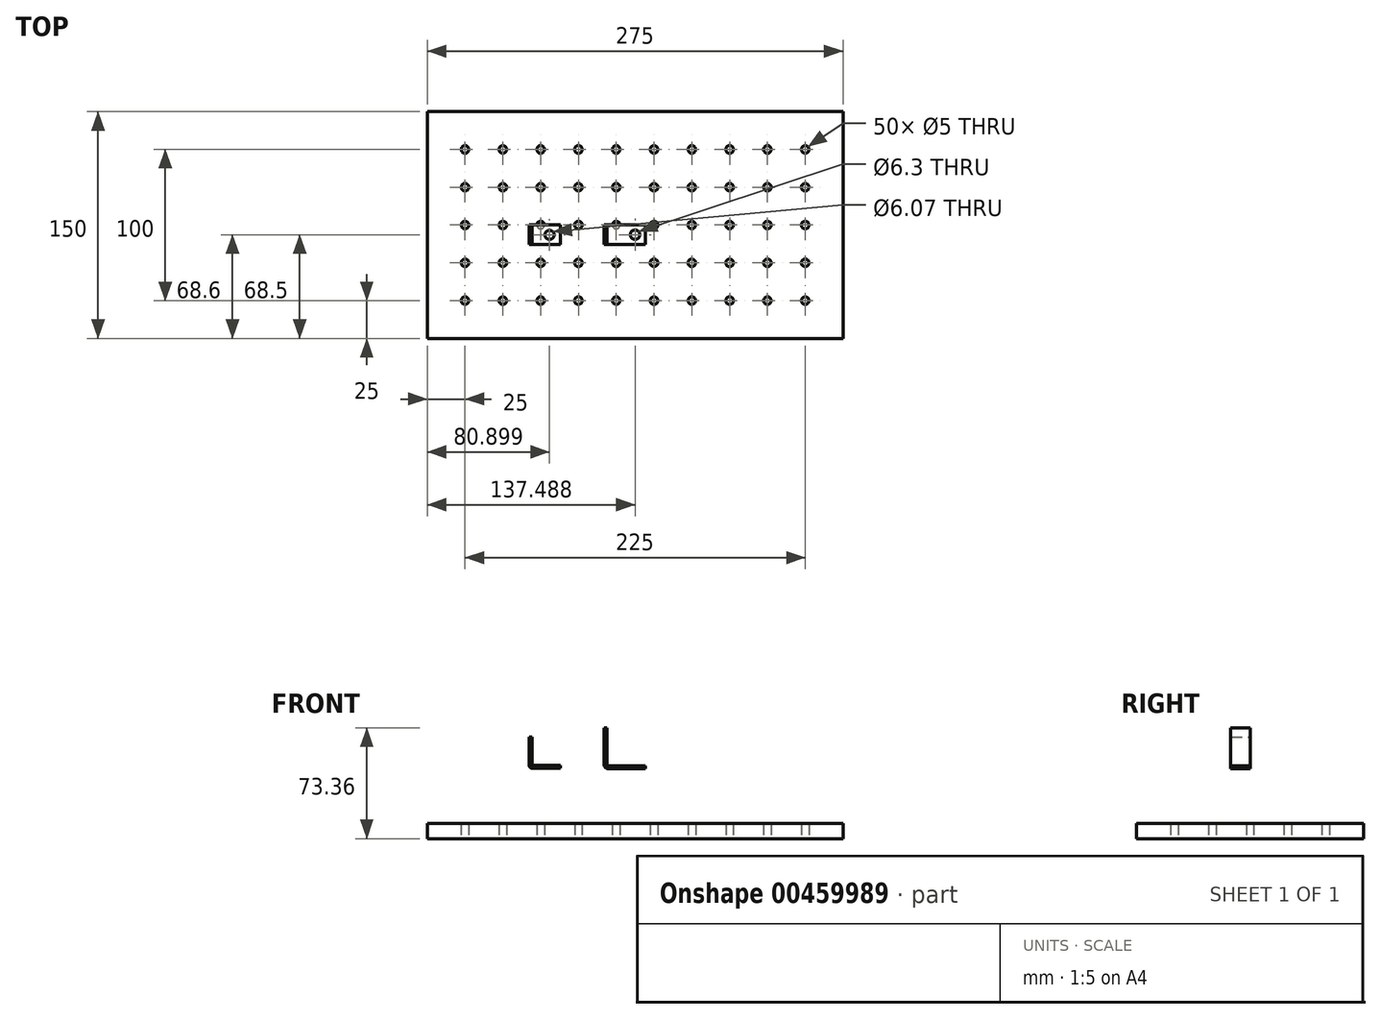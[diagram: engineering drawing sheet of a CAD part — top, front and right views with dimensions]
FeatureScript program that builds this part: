
annotation { "Feature Type Name" : "Feature", "Feature Type Description" : "" }
export const myFeature = defineFeature(function(context is Context, id is Id, definition is map)
    precondition{}
    {
        {
            var Q0;
            Q0=qCreatedBy(makeId("Top.planeOp"),FACE);
            var sketch = newSketch(context, id + "F0", { "sketchPlane" : qUnion([Q0])});
            skLineSegment(sketch, "E0.bottom", {"start": v(-137.5, 75) * mm, "end": v(137.5, 75) * mm});
            skLineSegment(sketch, "E0.top", {"start": v(-137.5, -75) * mm, "end": v(137.5, -75) * mm});
            skLineSegment(sketch, "E0.left", {"start": v(-137.5, 75) * mm, "end": v(-137.5, -75) * mm});
            skLineSegment(sketch, "E0.right", {"start": v(137.5, 75) * mm, "end": v(137.5, -75) * mm});
            skPoint(sketch, "E0.middle", {"position": v(0, 0) * mm});
            skCircle(sketch, "E1", {"center": v(-112.5, 50) * mm, "radius": 2.5 * mm});
            skCircle(sketch, "E2.0.1.0", {"center": v(-112.5, 25) * mm, "radius": 2.5 * mm});
            skCircle(sketch, "E2.0.2.0", {"center": v(-112.5, 0) * mm, "radius": 2.5 * mm});
            skCircle(sketch, "E2.0.3.0", {"center": v(-112.5, -25) * mm, "radius": 2.5 * mm});
            skCircle(sketch, "E2.0.4.0", {"center": v(-112.5, -50) * mm, "radius": 2.5 * mm});
            skCircle(sketch, "E2.1.0.0", {"center": v(-87.5, 50) * mm, "radius": 2.5 * mm});
            skCircle(sketch, "E2.1.1.0", {"center": v(-87.5, 25) * mm, "radius": 2.5 * mm});
            skCircle(sketch, "E2.1.2.0", {"center": v(-87.5, 0) * mm, "radius": 2.5 * mm});
            skCircle(sketch, "E2.1.3.0", {"center": v(-87.5, -25) * mm, "radius": 2.5 * mm});
            skCircle(sketch, "E2.1.4.0", {"center": v(-87.5, -50) * mm, "radius": 2.5 * mm});
            skCircle(sketch, "E2.2.0.0", {"center": v(-62.5, 50) * mm, "radius": 2.5 * mm});
            skCircle(sketch, "E2.2.1.0", {"center": v(-62.5, 25) * mm, "radius": 2.5 * mm});
            skCircle(sketch, "E2.2.2.0", {"center": v(-62.5, 0) * mm, "radius": 2.5 * mm});
            skCircle(sketch, "E2.2.3.0", {"center": v(-62.5, -25) * mm, "radius": 2.5 * mm});
            skCircle(sketch, "E2.2.4.0", {"center": v(-62.5, -50) * mm, "radius": 2.5 * mm});
            skCircle(sketch, "E2.3.0.0", {"center": v(-37.5, 50) * mm, "radius": 2.5 * mm});
            skCircle(sketch, "E2.3.1.0", {"center": v(-37.5, 25) * mm, "radius": 2.5 * mm});
            skCircle(sketch, "E2.3.2.0", {"center": v(-37.5, 0) * mm, "radius": 2.5 * mm});
            skCircle(sketch, "E2.3.3.0", {"center": v(-37.5, -25) * mm, "radius": 2.5 * mm});
            skCircle(sketch, "E2.3.4.0", {"center": v(-37.5, -50) * mm, "radius": 2.5 * mm});
            skCircle(sketch, "E2.4.0.0", {"center": v(-12.5, 50) * mm, "radius": 2.5 * mm});
            skCircle(sketch, "E2.4.1.0", {"center": v(-12.5, 25) * mm, "radius": 2.5 * mm});
            skCircle(sketch, "E2.4.2.0", {"center": v(-12.5, 0) * mm, "radius": 2.5 * mm});
            skCircle(sketch, "E2.4.3.0", {"center": v(-12.5, -25) * mm, "radius": 2.5 * mm});
            skCircle(sketch, "E2.4.4.0", {"center": v(-12.5, -50) * mm, "radius": 2.5 * mm});
            skCircle(sketch, "E2.5.0.0", {"center": v(12.5, 50) * mm, "radius": 2.5 * mm});
            skCircle(sketch, "E2.5.1.0", {"center": v(12.5, 25) * mm, "radius": 2.5 * mm});
            skCircle(sketch, "E2.5.2.0", {"center": v(12.5, 0) * mm, "radius": 2.5 * mm});
            skCircle(sketch, "E2.5.3.0", {"center": v(12.5, -25) * mm, "radius": 2.5 * mm});
            skCircle(sketch, "E2.5.4.0", {"center": v(12.5, -50) * mm, "radius": 2.5 * mm});
            skCircle(sketch, "E2.6.0.0", {"center": v(37.5, 50) * mm, "radius": 2.5 * mm});
            skCircle(sketch, "E2.6.1.0", {"center": v(37.5, 25) * mm, "radius": 2.5 * mm});
            skCircle(sketch, "E2.6.2.0", {"center": v(37.5, 0) * mm, "radius": 2.5 * mm});
            skCircle(sketch, "E2.6.3.0", {"center": v(37.5, -25) * mm, "radius": 2.5 * mm});
            skCircle(sketch, "E2.6.4.0", {"center": v(37.5, -50) * mm, "radius": 2.5 * mm});
            skCircle(sketch, "E2.7.0.0", {"center": v(62.5, 50) * mm, "radius": 2.5 * mm});
            skCircle(sketch, "E2.7.1.0", {"center": v(62.5, 25) * mm, "radius": 2.5 * mm});
            skCircle(sketch, "E2.7.2.0", {"center": v(62.5, 0) * mm, "radius": 2.5 * mm});
            skCircle(sketch, "E2.7.3.0", {"center": v(62.5, -25) * mm, "radius": 2.5 * mm});
            skCircle(sketch, "E2.7.4.0", {"center": v(62.5, -50) * mm, "radius": 2.5 * mm});
            skCircle(sketch, "E2.8.0.0", {"center": v(87.5, 50) * mm, "radius": 2.5 * mm});
            skCircle(sketch, "E2.8.1.0", {"center": v(87.5, 25) * mm, "radius": 2.5 * mm});
            skCircle(sketch, "E2.8.2.0", {"center": v(87.5, 0) * mm, "radius": 2.5 * mm});
            skCircle(sketch, "E2.8.3.0", {"center": v(87.5, -25) * mm, "radius": 2.5 * mm});
            skCircle(sketch, "E2.8.4.0", {"center": v(87.5, -50) * mm, "radius": 2.5 * mm});
            skCircle(sketch, "E2.9.0.0", {"center": v(112.5, 50) * mm, "radius": 2.5 * mm});
            skCircle(sketch, "E2.9.1.0", {"center": v(112.5, 25) * mm, "radius": 2.5 * mm});
            skCircle(sketch, "E2.9.2.0", {"center": v(112.5, 0) * mm, "radius": 2.5 * mm});
            skCircle(sketch, "E2.9.3.0", {"center": v(112.5, -25) * mm, "radius": 2.5 * mm});
            skCircle(sketch, "E2.9.4.0", {"center": v(112.5, -50) * mm, "radius": 2.5 * mm});
            skLineSegment(sketch, "E2.direction1", {"start": v(-112.5, 50) * mm, "end": v(-87.5, 50) * mm, "construction": true});
            skLineSegment(sketch, "E2.direction2", {"start": v(-112.5, 50) * mm, "end": v(-112.5, 25) * mm, "construction": true});
            skSolve(sketch);
        }
        {
            var Q0;
            Q0 = qSketchRegion(id + "F0", true);
            extrude(context, id + "F1", {"entities" : qUnion([Q0]), "depth" : 10 * mm, "offsetDistance" : 25 * mm});
        }
        {
            var Q0;
            Q0=qCreatedBy(makeId("Front.planeOp"),FACE);
            var sketch = newSketch(context, id + "F2", { "sketchPlane" : qUnion([Q0])});
            skLineSegment(sketch, "E3.bottom", {"start": v(-70.15, 67.24) * mm, "end": v(-68.27, 67.24) * mm});
            skLineSegment(sketch, "E3.top", {"start": v(-70.15, 48.86) * mm, "end": v(-68.27, 48.86) * mm});
            skLineSegment(sketch, "E3.left", {"start": v(-70.15, 67.24) * mm, "end": v(-70.15, 48.86) * mm});
            skLineSegment(sketch, "E3.right", {"start": v(-68.27, 67.24) * mm, "end": v(-68.27, 48.86) * mm});
            skLineSegment(sketch, "E4.bottom", {"start": v(-67.78, 48.37) * mm, "end": v(-49.4, 48.37) * mm});
            skLineSegment(sketch, "E4.top", {"start": v(-67.78, 46.49) * mm, "end": v(-49.4, 46.49) * mm});
            skLineSegment(sketch, "E4.left", {"start": v(-67.78, 48.37) * mm, "end": v(-67.78, 46.49) * mm});
            skLineSegment(sketch, "E4.right", {"start": v(-49.4, 48.37) * mm, "end": v(-49.4, 46.49) * mm});
            skLineSegment(sketch, "E5.bottom", {"start": v(-67.78, 48.86) * mm, "end": v(-70.15, 48.86) * mm, "construction": true});
            skLineSegment(sketch, "E5.top", {"start": v(-67.78, 46.49) * mm, "end": v(-70.15, 46.49) * mm, "construction": true});
            skLineSegment(sketch, "E5.left", {"start": v(-67.78, 48.86) * mm, "end": v(-67.78, 46.49) * mm, "construction": true});
            skLineSegment(sketch, "E5.right", {"start": v(-70.15, 48.86) * mm, "end": v(-70.15, 46.49) * mm, "construction": true});
            skArc(sketch, "E6", {"start": v(-68.27, 48.86) * mm, "mid": v(-68.13, 48.51) * mm, "end": v(-67.78, 48.37) * mm});
            skArc(sketch, "E7", {"start": v(-70.15, 48.86) * mm, "mid": v(-69.46, 47.18) * mm, "end": v(-67.78, 46.49) * mm});
            skSolve(sketch);
        }
        {
            var Q0;
            Q0 = qSketchRegion(id + "F2", true);
            extrude(context, id + "F3", {"entities" : qUnion([Q0]), "depth" : 13 * mm, "offsetDistance" : 25 * mm});
        }
        {
            var Q0;
            Q0=qCreatedBy(makeId("Front.planeOp"),FACE);
            var sketch = newSketch(context, id + "F4", { "sketchPlane" : qUnion([Q0])});
            skLineSegment(sketch, "E8.bottom", {"start": v(-20.55, 73.36) * mm, "end": v(-18.65, 73.36) * mm});
            skLineSegment(sketch, "E8.top", {"start": v(-20.55, 49.2) * mm, "end": v(-18.65, 49.2) * mm});
            skLineSegment(sketch, "E8.left", {"start": v(-20.55, 73.36) * mm, "end": v(-20.55, 49.2) * mm});
            skLineSegment(sketch, "E8.right", {"start": v(-18.65, 73.36) * mm, "end": v(-18.65, 49.2) * mm});
            skLineSegment(sketch, "E9.bottom", {"start": v(-17.6, 48.15) * mm, "end": v(6.89, 48.15) * mm});
            skLineSegment(sketch, "E9.top", {"start": v(-17.6, 46.25) * mm, "end": v(6.89, 46.25) * mm});
            skLineSegment(sketch, "E9.left", {"start": v(-17.6, 48.15) * mm, "end": v(-17.6, 46.25) * mm});
            skLineSegment(sketch, "E9.right", {"start": v(6.89, 48.15) * mm, "end": v(6.89, 46.25) * mm});
            skLineSegment(sketch, "E10.bottom", {"start": v(-20.55, 46.25) * mm, "end": v(-17.6, 46.25) * mm, "construction": true});
            skLineSegment(sketch, "E10.top", {"start": v(-20.55, 49.2) * mm, "end": v(-17.6, 49.2) * mm, "construction": true});
            skLineSegment(sketch, "E10.left", {"start": v(-20.55, 46.25) * mm, "end": v(-20.55, 49.2) * mm, "construction": true});
            skLineSegment(sketch, "E10.right", {"start": v(-17.6, 46.25) * mm, "end": v(-17.6, 49.2) * mm, "construction": true});
            skArc(sketch, "E11", {"start": v(-18.65, 49.2) * mm, "mid": v(-18.34, 48.46) * mm, "end": v(-17.6, 48.15) * mm});
            skArc(sketch, "E12", {"start": v(-20.55, 49.2) * mm, "mid": v(-19.69, 47.11) * mm, "end": v(-17.6, 46.25) * mm});
            skSolve(sketch);
        }
        {
            var Q0;
            Q0 = qSketchRegion(id + "F4", true);
            extrude(context, id + "F5", {"entities" : qUnion([Q0]), "depth" : 12.8 * mm, "offsetDistance" : 25 * mm});
        }
        {
            var Q0;
            Q0=makeQuery(id+"F5.opExtrude","SWEPT_FACE",FACE,{"disambiguationData":[OSD([sQuery(id+"F4.wireOp",EDGE,"E9.bottom")])]});
            var sketch = newSketch(context, id + "F6", { "sketchPlane" : qUnion([Q0])});
            skCircle(sketch, "E13", {"center": v(-0.01, -6.4) * mm, "radius": 3.15 * mm});
            skPoint(sketch, "E14", {"position": v(6.89, -6.4) * mm});
            skSolve(sketch);
        }
        {
            var Q0;
            Q0 = qSketchRegion(id + "F6", true);
            extrude(context, id + "F7", {"entities" : qUnion([Q0]), "operationType" : NewBodyOperationType.REMOVE, "endBound" : BoundingType.UP_TO_NEXT, "oppositeDirection" : true, "depth" : 25 * mm, "offsetDistance" : 25 * mm});
        }
        {
            var Q0;
            Q0=makeQuery(id+"F3.opExtrude","SWEPT_FACE",FACE,{"disambiguationData":[OSD([sQuery(id+"F2.wireOp",EDGE,"E4.bottom")])]});
            var sketch = newSketch(context, id + "F8", { "sketchPlane" : qUnion([Q0])});
            skCircle(sketch, "E15", {"center": v(-56.6, -6.5) * mm, "radius": 3.04 * mm});
            skPoint(sketch, "E16", {"position": v(-49.4, -6.5) * mm});
            skSolve(sketch);
        }
        {
            var Q0;
            Q0 = qSketchRegion(id + "F8", true);
            extrude(context, id + "F9", {"entities" : qUnion([Q0]), "operationType" : NewBodyOperationType.REMOVE, "endBound" : BoundingType.UP_TO_NEXT, "oppositeDirection" : true, "depth" : 25 * mm, "offsetDistance" : 25 * mm});
        }
    });
